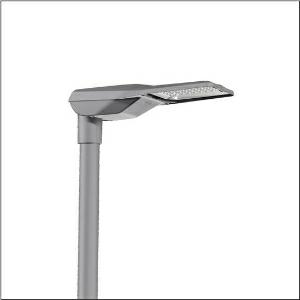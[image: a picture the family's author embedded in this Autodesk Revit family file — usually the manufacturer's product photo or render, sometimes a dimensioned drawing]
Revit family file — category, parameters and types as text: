
# Revit family: streetlight_sl_21_iq_mini___stw1_0a_5xe2e31g08gb_0d22
name_source: partatom
category: Lighting Fixtures
units: mm (PartAtom-declared; Revit-internal decimal feet)

## family parameters
Cut with Voids When Loaded = No
Host = Face
Light Source = No
Part Type = Normal
Room Calculation Point = No
Round Connector Dimension = Use Diameter
Shared = No

## types (1)
- --- (1 x LED, 5680 lm, 37.1 W, 3000K)
    Apparent Load = 37 VA
    CIE Flux Codes = 38 75 98 100 100
    Color Rendering = 70
    Color Temperature = 3000K
    Default Elevation = 1800 mm
    Description = Streetlight SL 21 mini, mast luminaire, primary light control with lens, of PMMA, primary optical cover: cover, of toughened safety glass, transparent, light distribution: STW1.0a, light emission: direct distribution, primary light characteristic: asymmetric, installation type: post-top, side-entry, LED, High Power LED, rated luminous flux: 5.680lm, luminous efficacy: 153lm/W, light colour: 730, colour temperature: 3000K, control gear: ECG iQ, control: Street-Remote, Auto-Match, Temp-Guard, Lumen-Switch, Night-Set, Smart-Wire, Light-Fading, Desk-Remote (wireless, voltage-free reading and setting of iQ features in the workshop via application-optimized NFC function/RFID function), optimised constant luminous flux control (CLO 2.0), mains connection: 220..240V, AC, 50/60Hz, start of lifetime: 37W, end of lifetime: 39W, reduction: 18W, luminaire housing, of diecast aluminium, powder-coated, Siteco® metallic grey (DB 702S), corrosivity category C5 according to DIN EN ISO 12944, length: 628mm, width: 235mm, height: 110mm, spigot size: 60/76mm (post-top) and 42/60/76mm (side-entry), mast flange for spigot size: 42mm: 5XC10008XM4, 60mm: 5XC10008XM2, 76/60mm: 5XC10108XM1, protection rating (complete): IP66, insulation class (complete): insulation class II (safety insulation), certification: CE, ENEC, VDE, impact resistance: IK09, permissible operating ambient temperature for outdoor applications: -40..+50°C, standard-compliant lighting for roads and squares, packaging unit: 1 piece

Light Distribution: STW1.0a
    Height = 110 mm
    Lamp = 1 x LED
    Lamp Light Flux = 5680 lm
    Lamp Power = 37.1 W
    Lamp count = 1
    Length = 625 mm
    Luminous efficacy = 153 lm/W
    Manufacturer = Siteco
    ModVariant = No
    Model = 5XE2E31G08GB
    Number of Poles = 1
    OnlyDefault = Yes
    Power Factor = 1
    Product Name = Streetlight SL 21 iQ mini | STW1.0a
    Product group = mast luminaire | pylon top
    ProductGroupID = 6100
    Protection Class = Protection class II
    Protection Degree = IP 66
    RLX_Detail_Level = 1
    RlxData = <blob elided: 92245 chars, md5=3e0e22ee>
    Socket = socket
    Standby Power = 0 W
    System Light Flux = 5680 lm
    System Power = 37 W
    Type Comments = factory setting: luminous flux: 100 % | dim-lin: 254 | 385 mA
    Type Image = l_1003519.jpg
    URL = http://relux.com
    VarID = @adj_104927
    Voltage = 0 V
    Weight = 0.00 kg
    Width = 234 mm

## geometry (parser evidence)
native form markers: Blend x4, Sweep x11
no freeform markers — native parametric forms only
